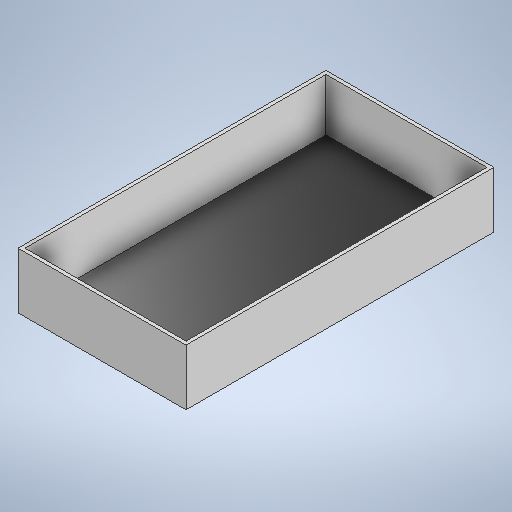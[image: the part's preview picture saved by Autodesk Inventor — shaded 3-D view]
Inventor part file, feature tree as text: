
AUTODESK INVENTOR PART (.ipt)
format: ipt  version: 2025 (Build 290162000, 162)  size: 268,288 bytes
history: native  units: in
note: dims shown in document units (in); Inventor stores cm internally (conversion verified against a paired STEP export)
features: extrude x4, sketch x3
ambient origin geometry x8: Origin, YZ Plane, XZ Plane, XY Plane, X Axis, Y Axis, Z Axis, Center Point
bodies: Solid1 (feature_tree)
feature tree (7):
  sketch  "Sketch1"  dims[d0=22.0in d1=12.0in]
  extrude  "Extrusion1"  Depth=12.0in
  extrude  "Extrusion2"  Depth=11.5in
  extrude  "Extrusion3"  Depth=4.0in TaperAngle=0.0deg
  extrude  "Extrusion4"  Depth=3.937in
  sketch  "Sketch2"  dims[d2=21.5in d3=11.5in]
  sketch  "Sketch3"  dims[d4=0.25in d5=0.0in d6=4.0in d7=0.0in d8=3.937in d9=0.7874in d10=1.9685in d11=0.0in d12=0.3937in d13=0.3937in d14=0.3937in d15=1.9685in d16=0.0in]
